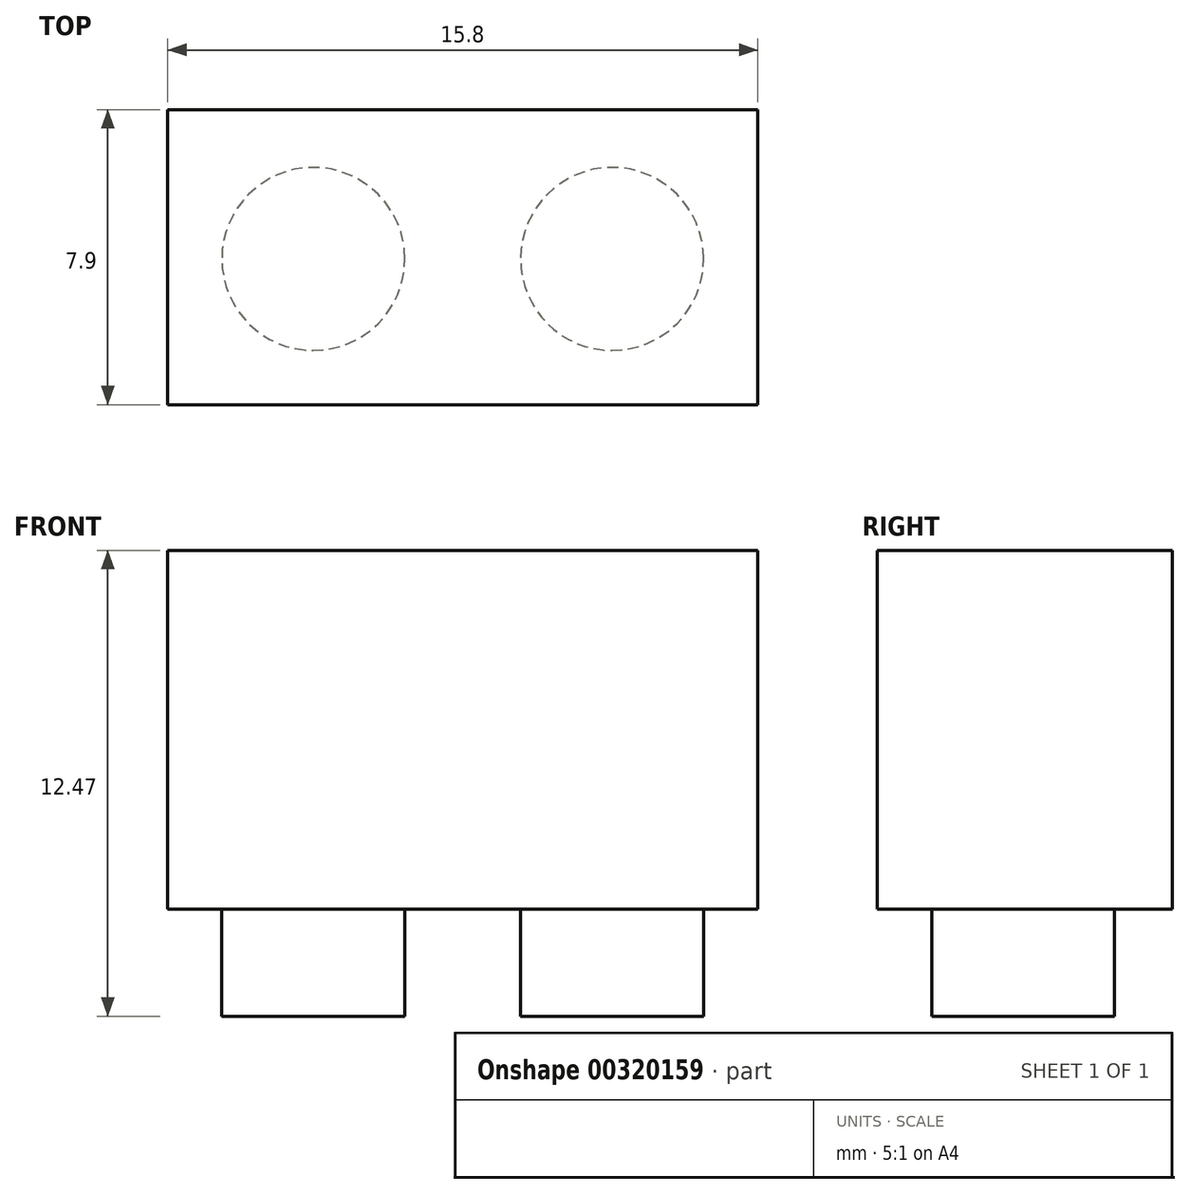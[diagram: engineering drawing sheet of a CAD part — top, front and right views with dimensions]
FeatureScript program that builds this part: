
annotation { "Feature Type Name" : "Feature", "Feature Type Description" : "" }
export const myFeature = defineFeature(function(context is Context, id is Id, definition is map)
    precondition{}
    {
        {
            var Q0;
            Q0=qCreatedBy(makeId("Top.planeOp"),FACE);
            var sketch = newSketch(context, id + "F0", { "sketchPlane" : qUnion([Q0])});
            skLineSegment(sketch, "E0.bottom", {"start": v(-15.8, 0) * mm, "end": v(0, 0) * mm});
            skLineSegment(sketch, "E0.top", {"start": v(-15.8, -7.9) * mm, "end": v(0, -7.9) * mm});
            skLineSegment(sketch, "E0.left", {"start": v(-15.8, 0) * mm, "end": v(-15.8, -7.9) * mm});
            skLineSegment(sketch, "E0.right", {"start": v(0, 0) * mm, "end": v(0, -7.9) * mm});
            skCircle(sketch, "E1", {"center": v(-11.9, -4) * mm, "radius": 2.45 * mm});
            skCircle(sketch, "E2", {"center": v(-3.9, -4) * mm, "radius": 2.45 * mm});
            skLineSegment(sketch, "E3", {"start": v(-15.8, -4) * mm, "end": v(-11.9, -4) * mm, "construction": true});
            skLineSegment(sketch, "E4", {"start": v(-11.9, -4) * mm, "end": v(-3.9, -4) * mm, "construction": true});
            skLineSegment(sketch, "E5", {"start": v(-3.9, -4) * mm, "end": v(0, -4) * mm, "construction": true});
            skSolve(sketch);
        }
        {
            var Q0;
            Q0=makeQuery(id+"F0.imprint","IMPRINT",FACE,{"disambiguationData":[TD([[makeQuery(id+"F0.imprint","IMPRINT",EDGE,{"derivedFrom":sQuery(id+"F0.wireOp",EDGE,"E0.bottom")}),-1.0]])]});
            var Q1;
            Q1=makeQuery(id+"F0.imprint","IMPRINT",FACE,{"disambiguationData":[TD([[makeQuery(id+"F0.imprint","IMPRINT",EDGE,{"derivedFrom":sQuery(id+"F0.wireOp",EDGE,"E1")}),1.0]])]});
            var Q2;
            Q2=makeQuery(id+"F0.imprint","IMPRINT",FACE,{"disambiguationData":[TD([[makeQuery(id+"F0.imprint","IMPRINT",EDGE,{"derivedFrom":sQuery(id+"F0.wireOp",EDGE,"E2")}),1.0]])]});
            extrude(context, id + "F1", {"entities" : qUnion([Q0, Q1, Q2]), "depth" : 9.6 * mm});
        }
        {
            var Q0;
            Q0=makeQuery(id+"F0.imprint","IMPRINT",FACE,{"disambiguationData":[TD([[makeQuery(id+"F0.imprint","IMPRINT",EDGE,{"derivedFrom":sQuery(id+"F0.wireOp",EDGE,"E2")}),1.0]])]});
            var Q1;
            Q1=makeQuery(id+"F0.imprint","IMPRINT",FACE,{"disambiguationData":[TD([[makeQuery(id+"F0.imprint","IMPRINT",EDGE,{"derivedFrom":sQuery(id+"F0.wireOp",EDGE,"E1")}),1.0]])]});
            var Q2;
            Q2=qSketchRegion(id+"F3",true);
            extrude(context, id + "F2", {"entities" : qUnion([Q0, Q1, Q2]), "operationType" : NewBodyOperationType.ADD, "oppositeDirection" : true, "depth" : 2.87 * mm});
        }
    });
